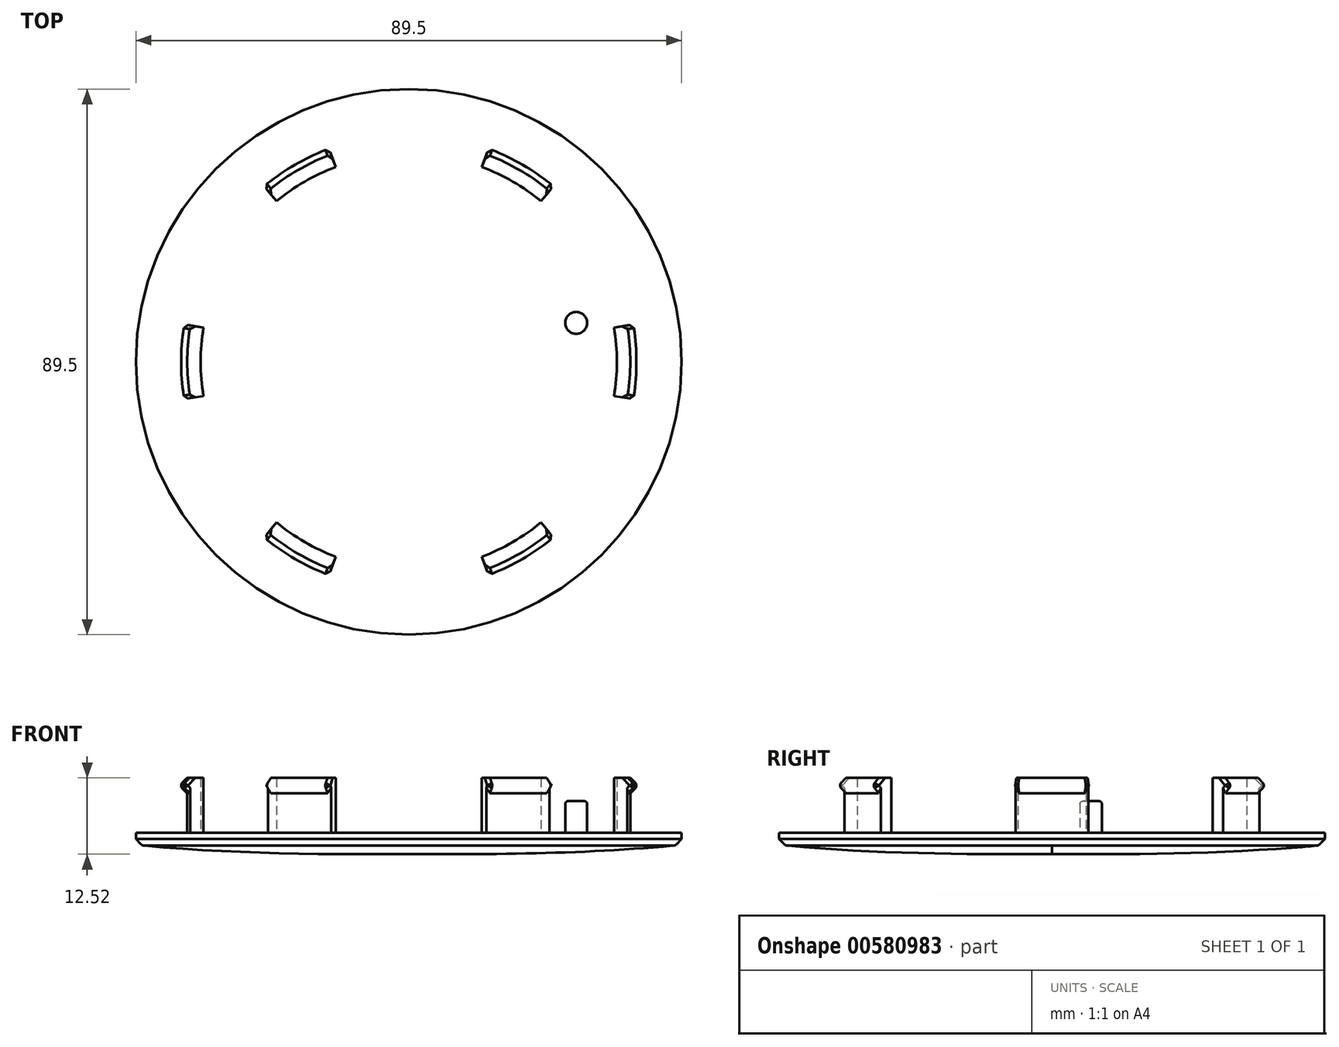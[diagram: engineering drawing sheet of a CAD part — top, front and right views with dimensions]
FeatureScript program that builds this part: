
annotation { "Feature Type Name" : "Feature", "Feature Type Description" : "" }
export const myFeature = defineFeature(function(context is Context, id is Id, definition is map)
    precondition{}
    {
        {
            var Q0;
            Q0=qCreatedBy(makeId("Top.planeOp"),FACE);
            var sketch = newSketch(context, id + "F0", { "sketchPlane" : qUnion([Q0])});
            skCircle(sketch, "E0", {"center": v(0, 0) * mm, "radius": 44.75 * mm});
            skCircle(sketch, "E1", {"center": v(27.45, 6.4) * mm, "radius": 1.8 * mm});
            skLineSegment(sketch, "E2", {"start": v(0, 44.75) * mm, "end": v(0, -44.75) * mm, "construction": true});
            skLineSegment(sketch, "E3", {"start": v(-44.75, 0) * mm, "end": v(44.75, 0) * mm, "construction": true});
            skLineSegment(sketch, "E4", {"start": v(29.25, 6.4) * mm, "end": v(29.25, 0) * mm});
            skLineSegment(sketch, "E5", {"start": v(27.45, 4.6) * mm, "end": v(0, 4.6) * mm});
            skArc(sketch, "E6", {"start": v(-35.84, 5.97) * mm, "mid": v(-36.34, 0) * mm, "end": v(-35.84, -5.97) * mm});
            skLineSegment(sketch, "E7", {"start": v(0, 0) * mm, "end": v(-35.84, 5.97) * mm, "construction": true});
            skLineSegment(sketch, "E8", {"start": v(0, 0) * mm, "end": v(-35.84, -5.97) * mm, "construction": true});
            skLineSegment(sketch, "E9", {"start": v(-35.84, 5.97) * mm, "end": v(-35.84, -5.97) * mm, "construction": true});
            skPoint(sketch, "E10", {"position": v(-35.84, 0) * mm});
            skArc(sketch, "E11.0", {"start": v(-33.67, 5.6) * mm, "mid": v(-34.13, 0) * mm, "end": v(-33.67, -5.6) * mm});
            skLineSegment(sketch, "E12", {"start": v(-35.84, 5.97) * mm, "end": v(-33.67, 5.6) * mm});
            skLineSegment(sketch, "E13", {"start": v(-35.84, -5.97) * mm, "end": v(-33.67, -5.6) * mm});
            skSolve(sketch);
        }
        {
            var Q0;
            Q0=makeQuery(id+"F0.imprint","IMPRINT",FACE,{"disambiguationData":[TD([[makeQuery(id+"F0.imprint","IMPRINT",EDGE,{"derivedFrom":sQuery(id+"F0.wireOp",EDGE,"E6")}),1.0]])]});
            extrude(context, id + "F1", {"entities" : qUnion([Q0]), "depth" : 9 * mm, "offsetDistance" : 25 * mm});
        }
        {
            var Q0;
            Q0=makeQuery(id+"F1.opExtrude","CAP_FACE",FACE,{"disambiguationData":[OSD([sQuery(id+"F0.wireOp",EDGE,"E6"),sQuery(id+"F0.wireOp",EDGE,"E11.0"),sQuery(id+"F0.wireOp",EDGE,"E12"),sQuery(id+"F0.wireOp",EDGE,"E13")])],"isStart":false});
            var sketch = newSketch(context, id + "F2", { "sketchPlane" : qUnion([Q0])});
            skArc(sketch, "E14.0", {"start": v(-36.83, 6.13) * mm, "mid": v(-37.34, 0) * mm, "end": v(-36.83, -6.13) * mm});
            skLineSegment(sketch, "E15", {"start": v(-36.83, 6.13) * mm, "end": v(-35.84, 5.97) * mm});
            skLineSegment(sketch, "E16", {"start": v(-36.83, -6.13) * mm, "end": v(-35.84, -5.97) * mm});
            skArc(sketch, "E17.0", {"start": v(-35.84, 5.97) * mm, "mid": v(-36.34, 0) * mm, "end": v(-35.84, -5.97) * mm});
            skSolve(sketch);
        }
        {
            var Q0;
            Q0=makeQuery(id+"F2.imprint","IMPRINT",FACE,{"disambiguationData":[TD([[makeQuery(id+"F2.imprint","IMPRINT",EDGE,{"derivedFrom":sQuery(id+"F2.wireOp",EDGE,"E14.0")}),1.0]])]});
            extrude(context, id + "F3", {"entities" : qUnion([Q0]), "operationType" : NewBodyOperationType.ADD, "oppositeDirection" : true, "depth" : 2.5 * mm, "offsetDistance" : 25 * mm});
        }
        {
            var Q0;
            Q0=makeQuery(id+"F3.opExtrude","CAP_EDGE",EDGE,{"disambiguationData":[OSD([sQuery(id+"F2.wireOp",EDGE,"E14.0")])],"isStart":false});
            var Q1;
            Q1=makeQuery(id+"F3.opExtrude","CAP_EDGE",EDGE,{"disambiguationData":[OSD([sQuery(id+"F2.wireOp",EDGE,"E14.0")])],"isStart":true});
            chamfer(context, id + "F4", {"entities" : qUnion([Q0, Q1]), "width" : 1 * mm, "tangentPropagation" : true});
        }
        {
            var Q0;
            {var subQ0=sQuery(id+"F2.wireOp",EDGE,"E14.0");Q0=makeQuery(id+"F4.opChamfer","BLEND_EDGE",EDGE,{"blendedFrom":[makeQuery(id+"F3.opExtrude","CAP_EDGE",EDGE,{"disambiguationData":[OSD([subQ0])],"isStart":true}),makeQuery(id+"F3.opExtrude","SWEPT_FACE",FACE,{"disambiguationData":[OSD([subQ0])]})],"blendedInto":[makeQuery(id+"F3.opExtrude","SWEPT_FACE",FACE,{"disambiguationData":[OSD([subQ0])]})]});}
            var Q1;
            {var subQ0=sQuery(id+"F2.wireOp",EDGE,"E14.0");Q1=makeQuery(id+"F4.opChamfer","BLEND_EDGE",EDGE,{"blendedFrom":[makeQuery(id+"F3.opExtrude","CAP_EDGE",EDGE,{"disambiguationData":[OSD([subQ0])],"isStart":false}),makeQuery(id+"F3.opExtrude","SWEPT_FACE",FACE,{"disambiguationData":[OSD([subQ0])]})],"blendedInto":[makeQuery(id+"F3.opExtrude","SWEPT_FACE",FACE,{"disambiguationData":[OSD([subQ0])]})]});}
            fillet(context, id + "F5", {"entities" : qUnion([Q0, Q1]), "radius" : 0.6 * mm, "tangentPropagation" : true, "allowEdgeOverflow" : false});
        }
        {
            var Q0;
            Q0=makeQuery(id+"F0.imprint","IMPRINT",FACE,{"disambiguationData":[TD([[makeQuery(id+"F0.imprint","IMPRINT",EDGE,{"derivedFrom":sQuery(id+"F0.wireOp",EDGE,"E0")}),1.0]])]});
            var Q1;
            Q1=makeQuery(id+"F0.imprint","IMPRINT",FACE,{"disambiguationData":[TD([[makeQuery(id+"F0.imprint","IMPRINT",EDGE,{"derivedFrom":sQuery(id+"F0.wireOp",EDGE,"E6")}),1.0]])]});
            var Q2;
            {var subQ0=sQuery(id+"F0.wireOp",EDGE,"E1");var subQ1=makeQuery(id+"F0.imprint","IMPRINT",VERTEX,{"disambiguationData":[OD(0.0)],"derivedFrom":subQ0});Q2=makeQuery(id+"F0.imprint","IMPRINT",FACE,{"disambiguationData":[TD([[makeQuery(id+"F0.imprint","IMPRINT",EDGE,{"disambiguationData":[TD([[subQ1,1.0]])],"derivedFrom":subQ0}),1.0]])]});}
            extrude(context, id + "F6", {"entities" : qUnion([Q0, Q1, Q2]), "oppositeDirection" : true, "depth" : 2 * mm, "offsetDistance" : 25 * mm});
        }
        {
            var Q0;
            Q0=qCreatedBy(makeId("Front.planeOp"),FACE);
            var sketch = newSketch(context, id + "F7", { "sketchPlane" : qUnion([Q0])});
            skLineSegment(sketch, "E18.0", {"start": v(0, -2) * mm, "end": v(44.75, -2) * mm});
            skLineSegment(sketch, "E19", {"start": v(0, -2) * mm, "end": v(0, -3.5) * mm});
            skFitSpline(sketch, "E20", {"points": [v(0, -3.5) * mm, v(44.75, -2) * mm], "startDerivative": vector(47.81, -0.25) * mm, "endDerivative": vector(44.57, 4.23) * mm});
            skLineSegment(sketch, "E21", {"start": v(0, 0) * mm, "end": v(0, -17.61) * mm, "construction": true});
            skSolve(sketch);
        }
        {
            var Q0;
            Q0=makeQuery(id+"F7.imprint","IMPRINT",FACE,{"disambiguationData":[TD([[makeQuery(id+"F7.imprint","IMPRINT",EDGE,{"derivedFrom":sQuery(id+"F7.wireOp",EDGE,"E18.0")}),-1.0]])]});
            var Q1;
            Q1=sQuery(id+"F7.wireOp",EDGE,"E21");
            revolve(context, id + "F8", {"operationType" : NewBodyOperationType.ADD, "entities" : qUnion([Q0]), "axis" : qUnion([Q1]), "revolveType" : RevolveType.FULL});
        }
        {
            var Q0;
            Q0=makeQuery(id+"F4.opChamfer","BLEND_EDGE",EDGE,{"blendedFrom":[makeQuery(id+"F3.opExtrude","CAP_EDGE",EDGE,{"disambiguationData":[OSD([sQuery(id+"F2.wireOp",EDGE,"E14.0")])],"isStart":true}),makeQuery(id+"F3.boolean.opBoolean","MERGE",FACE,{"derivedFrom":[makeQuery(id+"F1.opExtrude","SWEPT_FACE",FACE,{"disambiguationData":[OSD([sQuery(id+"F0.wireOp",EDGE,"E13")])]}),makeQuery(id+"F3.opExtrude","SWEPT_FACE",FACE,{"disambiguationData":[OSD([sQuery(id+"F2.wireOp",EDGE,"E16")])]})]})],"blendedInto":[makeQuery(id+"F3.boolean.opBoolean","MERGE",FACE,{"derivedFrom":[makeQuery(id+"F1.opExtrude","SWEPT_FACE",FACE,{"disambiguationData":[OSD([sQuery(id+"F0.wireOp",EDGE,"E13")])]}),makeQuery(id+"F3.opExtrude","SWEPT_FACE",FACE,{"disambiguationData":[OSD([sQuery(id+"F2.wireOp",EDGE,"E16")])]})]})]});
            var Q1;
            {var subQ0=sQuery(id+"F2.wireOp",EDGE,"E14.0");Q1=makeQuery(id+"F5.opFillet","BLEND_EDGE",EDGE,{"blendedFrom":[makeQuery(id+"F4.opChamfer","BLEND_EDGE",EDGE,{"blendedFrom":[makeQuery(id+"F3.opExtrude","CAP_EDGE",EDGE,{"disambiguationData":[OSD([subQ0])],"isStart":true}),makeQuery(id+"F3.opExtrude","SWEPT_FACE",FACE,{"disambiguationData":[OSD([subQ0])]})],"blendedInto":[makeQuery(id+"F3.opExtrude","SWEPT_FACE",FACE,{"disambiguationData":[OSD([subQ0])]})]}),makeQuery(id+"F3.boolean.opBoolean","MERGE",FACE,{"derivedFrom":[makeQuery(id+"F1.opExtrude","SWEPT_FACE",FACE,{"disambiguationData":[OSD([sQuery(id+"F0.wireOp",EDGE,"E12")])]}),makeQuery(id+"F3.opExtrude","SWEPT_FACE",FACE,{"disambiguationData":[OSD([sQuery(id+"F2.wireOp",EDGE,"E15")])]})]})],"blendedInto":[makeQuery(id+"F3.boolean.opBoolean","MERGE",FACE,{"derivedFrom":[makeQuery(id+"F1.opExtrude","SWEPT_FACE",FACE,{"disambiguationData":[OSD([sQuery(id+"F0.wireOp",EDGE,"E12")])]}),makeQuery(id+"F3.opExtrude","SWEPT_FACE",FACE,{"disambiguationData":[OSD([sQuery(id+"F2.wireOp",EDGE,"E15")])]})]})]});}
            chamfer(context, id + "F9", {"entities" : qUnion([Q0, Q1]), "width" : 0.6 * mm, "tangentPropagation" : true});
        }
        {
            var Q0;
            Q0=makeQuery(id+"F1.opExtrude","SWEPT_BODY",BODY,{"disambiguationData":[OSD([sQuery(id+"F0.wireOp",EDGE,"E6"),sQuery(id+"F0.wireOp",EDGE,"E11.0"),sQuery(id+"F0.wireOp",EDGE,"E12"),sQuery(id+"F0.wireOp",EDGE,"E13")])]});
            var Q1;
            Q1=sQuery(id+"F7.wireOp",EDGE,"E21");
            circularPattern(context, id + "F10", {"operationType" : NewBodyOperationType.ADD, "entities" : qUnion([Q0]), "axis" : qUnion([Q1]), "angle" : 360 * degree, "instanceCount" : 6, "equalSpace" : true});
        }
        {
            var Q0;
            {var subQ0=sQuery(id+"F0.wireOp",EDGE,"E1");var subQ1=makeQuery(id+"F0.imprint","IMPRINT",VERTEX,{"disambiguationData":[OD(0.0)],"derivedFrom":subQ0});Q0=makeQuery(id+"F0.imprint","IMPRINT",FACE,{"disambiguationData":[TD([[makeQuery(id+"F0.imprint","IMPRINT",EDGE,{"disambiguationData":[TD([[subQ1,1.0]])],"derivedFrom":subQ0}),1.0]])]});}
            extrude(context, id + "F11", {"entities" : qUnion([Q0]), "operationType" : NewBodyOperationType.ADD, "depth" : 5.2 * mm, "offsetDistance" : 25 * mm});
        }
        {
            var Q0;
            Q0=makeQuery(id+"F8.boolean.opBoolean","MERGE",EDGE,{"derivedFrom":[makeQuery(id+"F6.opExtrude","CAP_EDGE",EDGE,{"disambiguationData":[OSD([sQuery(id+"F0.wireOp",EDGE,"E0")])],"isStart":false}),makeQuery(id+"F8.opRevolve","SWEPT_EDGE",EDGE,{"disambiguationData":[OSD([sQuery(id+"F7.wireOp",EDGE,"E18.0"),sQuery(id+"F7.wireOp",EDGE,"E20")])]})]});
            chamfer(context, id + "F12", {"entities" : qUnion([Q0]), "width" : 1.1 * mm, "tangentPropagation" : true});
        }
        {
            var Q0;
            {var subQ0=sQuery(id+"F7.wireOp",EDGE,"E20");Q0=makeQuery(id+"F12.opChamfer","BLEND_EDGE",EDGE,{"blendedFrom":[makeQuery(id+"F8.boolean.opBoolean","MERGE",EDGE,{"derivedFrom":[makeQuery(id+"F6.opExtrude","CAP_EDGE",EDGE,{"disambiguationData":[OSD([sQuery(id+"F0.wireOp",EDGE,"E0")])],"isStart":false}),makeQuery(id+"F8.opRevolve","SWEPT_EDGE",EDGE,{"disambiguationData":[OSD([sQuery(id+"F7.wireOp",EDGE,"E18.0"),subQ0])]})]}),makeQuery(id+"F8.opRevolve","SWEPT_FACE",FACE,{"disambiguationData":[OSD([subQ0])]})],"blendedInto":[makeQuery(id+"F8.opRevolve","SWEPT_FACE",FACE,{"disambiguationData":[OSD([subQ0])]})]});}
            fillet(context, id + "F13", {"entities" : qUnion([Q0]), "radius" : 1 * mm, "tangentPropagation" : true, "allowEdgeOverflow" : false});
        }
        {
            var Q0;
            Q0=makeQuery(id+"F11.opExtrude","CAP_EDGE",EDGE,{"disambiguationData":[OSD([sQuery(id+"F0.wireOp",EDGE,"E1")])],"isStart":false});
            fillet(context, id + "F14", {"entities" : qUnion([Q0]), "radius" : 0.5 * mm, "tangentPropagation" : true, "allowEdgeOverflow" : false});
        }
    });
